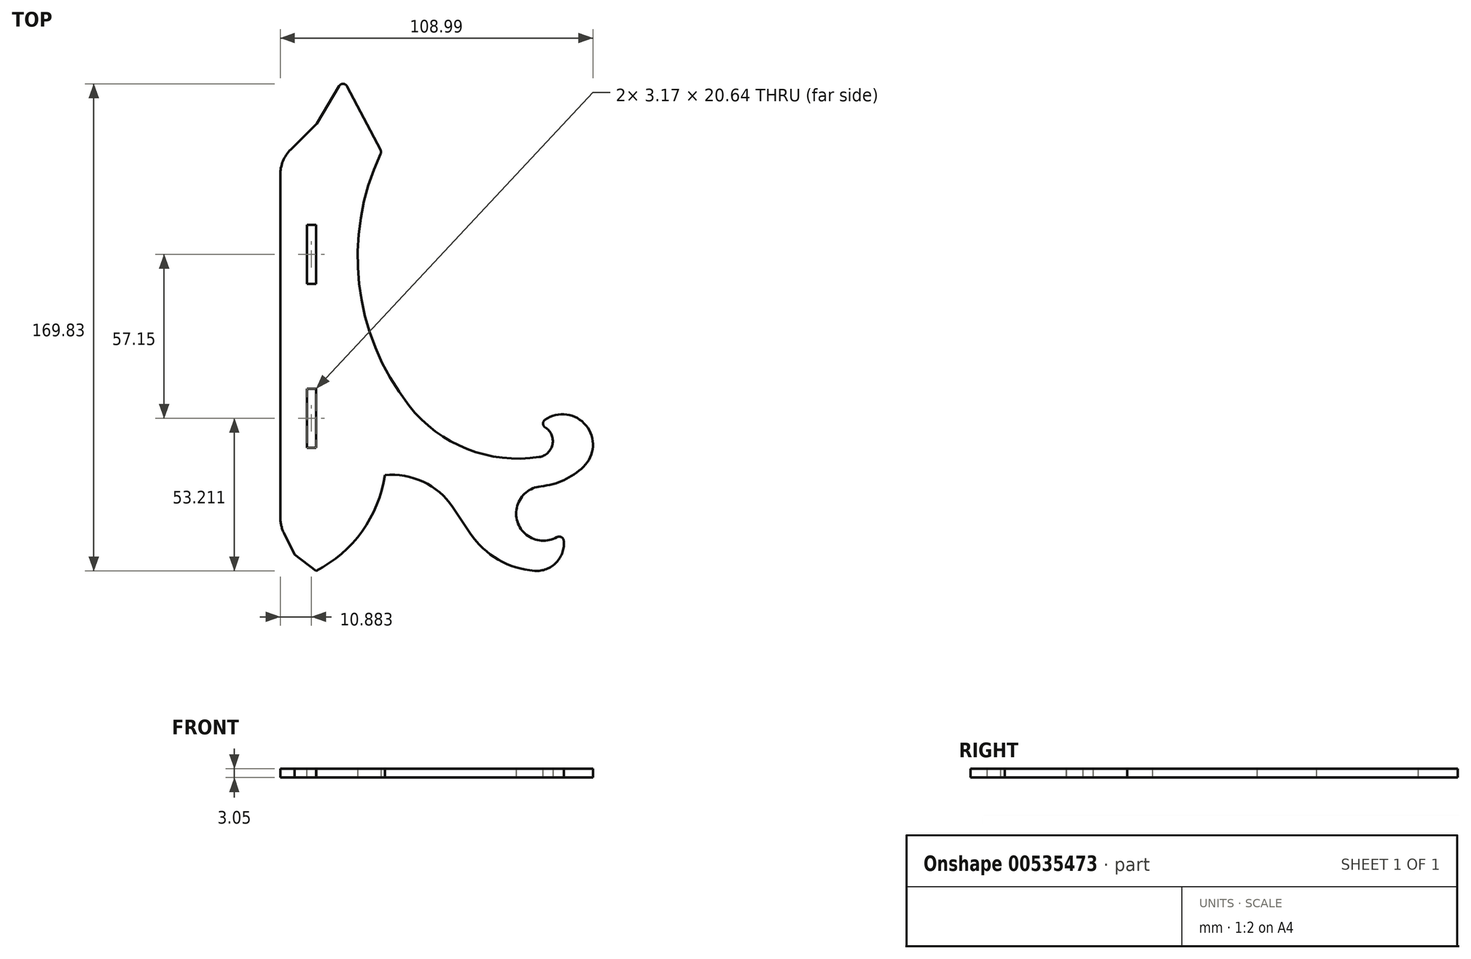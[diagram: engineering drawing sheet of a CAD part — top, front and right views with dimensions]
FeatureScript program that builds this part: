
annotation { "Feature Type Name" : "Feature", "Feature Type Description" : "" }
export const myFeature = defineFeature(function(context is Context, id is Id, definition is map)
    precondition{}
    {
        {
            var Q0;
            Q0=qCreatedBy(makeId("Top.planeOp"),FACE);
            var sketch = newSketch(context, id + "F0", { "sketchPlane" : qUnion([Q0])});
            skLineSegment(sketch, "E0", {"start": v(0, 0) * mm, "end": v(0, 155.58) * mm});
            skLineSegment(sketch, "E1", {"start": v(0, 155.58) * mm, "end": v(9.52, 171.45) * mm});
            skLineSegment(sketch, "E2", {"start": v(9.53, 171.45) * mm, "end": v(22.86, 146.05) * mm});
            skArc(sketch, "E3", {"start": v(0, 0) * mm, "mid": v(16.07, 13.73) * mm, "end": v(23.97, 33.34) * mm});
            skArc(sketch, "E4", {"start": v(47.62, 22.23) * mm, "mid": v(37.34, 31.06) * mm, "end": v(23.97, 33.34) * mm});
            skLineSegment(sketch, "E5", {"start": v(47.62, 22.23) * mm, "end": v(53.82, 13) * mm});
            skArc(sketch, "E6", {"start": v(53.82, 13) * mm, "mid": v(63.51, 3.92) * mm, "end": v(76.2, 0) * mm});
            skArc(sketch, "E7", {"start": v(76.2, 0) * mm, "mid": v(84.56, 3.86) * mm, "end": v(85.73, 13) * mm});
            skArc(sketch, "E8", {"start": v(78.35, 29.47) * mm, "mid": v(70.6, 16.1) * mm, "end": v(85.72, 13) * mm});
            skArc(sketch, "E9", {"start": v(78.35, 29.47) * mm, "mid": v(86.36, 31.63) * mm, "end": v(93.22, 36.28) * mm});
            skArc(sketch, "E10", {"start": v(22.86, 146.05) * mm, "mid": v(15, 100.47) * mm, "end": v(32.42, 57.61) * mm});
            skArc(sketch, "E11", {"start": v(32.42, 57.61) * mm, "mid": v(52.67, 42.5) * mm, "end": v(77.79, 39.69) * mm});
            skArc(sketch, "E12", {"start": v(77.79, 39.69) * mm, "mid": v(82.55, 45.24) * mm, "end": v(77.79, 50.8) * mm});
            skArc(sketch, "E13", {"start": v(93.22, 36.28) * mm, "mid": v(93.18, 51.7) * mm, "end": v(77.79, 50.8) * mm});
            skSolve(sketch);
        }
        {
            var Q0;
            Q0=makeQuery(id+"F0.imprint","IMPRINT",FACE,{"disambiguationData":[TD([[makeQuery(id+"F0.imprint","IMPRINT",EDGE,{"derivedFrom":sQuery(id+"F0.wireOp",EDGE,"E0")}),-1.0]])]});
            extrude(context, id + "F1", {"entities" : qUnion([Q0]), "depth" : 3.05 * mm, "offsetDistance" : 25.4 * mm});
        }
        {
            var Q0;
            Q0=makeQuery(id+"F1.opExtrude","SWEPT_EDGE",EDGE,{"disambiguationData":[OSD([sQuery(id+"F0.wireOp",EDGE,"E7"),sQuery(id+"F0.wireOp",EDGE,"E8")])]});
            var Q1;
            Q1=makeQuery(id+"F1.opExtrude","SWEPT_EDGE",EDGE,{"disambiguationData":[OSD([sQuery(id+"F0.wireOp",EDGE,"E2"),sQuery(id+"F0.wireOp",EDGE,"E10")])]});
            var Q2;
            Q2=makeQuery(id+"F1.opExtrude","SWEPT_EDGE",EDGE,{"disambiguationData":[OSD([sQuery(id+"F0.wireOp",EDGE,"E1"),sQuery(id+"F0.wireOp",EDGE,"E2")])]});
            var Q3;
            Q3=makeQuery(id+"F1.opExtrude","SWEPT_EDGE",EDGE,{"disambiguationData":[OSD([sQuery(id+"F0.wireOp",EDGE,"E0"),sQuery(id+"F0.wireOp",EDGE,"E1")])]});
            var Q4;
            Q4=makeQuery(id+"F1.opExtrude","SWEPT_EDGE",EDGE,{"disambiguationData":[OSD([sQuery(id+"F0.wireOp",EDGE,"E12"),sQuery(id+"F0.wireOp",EDGE,"E13")])]});
            fillet(context, id + "F2", {"entities" : qUnion([Q0, Q1, Q2, Q3, Q4]), "radius" : 1.59 * mm, "tangentPropagation" : true, "allowEdgeOverflow" : false});
        }
        {
            var Q0;
            Q0=makeQuery(id+"F1.opExtrude","SWEPT_BODY",BODY,{"disambiguationData":[OSD([sQuery(id+"F0.wireOp",EDGE,"E0"),sQuery(id+"F0.wireOp",EDGE,"E1"),sQuery(id+"F0.wireOp",EDGE,"E2"),sQuery(id+"F0.wireOp",EDGE,"E3"),sQuery(id+"F0.wireOp",EDGE,"E4"),sQuery(id+"F0.wireOp",EDGE,"E5"),sQuery(id+"F0.wireOp",EDGE,"E6"),sQuery(id+"F0.wireOp",EDGE,"E7"),sQuery(id+"F0.wireOp",EDGE,"E8"),sQuery(id+"F0.wireOp",EDGE,"E9"),sQuery(id+"F0.wireOp",EDGE,"E10"),sQuery(id+"F0.wireOp",EDGE,"E11"),sQuery(id+"F0.wireOp",EDGE,"E12"),sQuery(id+"F0.wireOp",EDGE,"E13")])]});
            transform(context, id + "F3", {"entities" : qUnion([Q0]), "transformType" : TransformType.TRANSLATION_3D, "dx" : 0 * mm, "dy" : 0 * mm, "dz" : 0 * mm, "makeCopy" : true});
        }
        {
            var Q0;
            Q0=makeQuery(id+"F1.opExtrude","CAP_FACE",FACE,{"disambiguationData":[OSD([sQuery(id+"F0.wireOp",EDGE,"E0"),sQuery(id+"F0.wireOp",EDGE,"E1"),sQuery(id+"F0.wireOp",EDGE,"E2"),sQuery(id+"F0.wireOp",EDGE,"E3"),sQuery(id+"F0.wireOp",EDGE,"E4"),sQuery(id+"F0.wireOp",EDGE,"E5"),sQuery(id+"F0.wireOp",EDGE,"E6"),sQuery(id+"F0.wireOp",EDGE,"E7"),sQuery(id+"F0.wireOp",EDGE,"E8"),sQuery(id+"F0.wireOp",EDGE,"E9"),sQuery(id+"F0.wireOp",EDGE,"E10"),sQuery(id+"F0.wireOp",EDGE,"E11"),sQuery(id+"F0.wireOp",EDGE,"E12"),sQuery(id+"F0.wireOp",EDGE,"E13")])],"isStart":false});
            var sketch = newSketch(context, id + "F4", { "sketchPlane" : qUnion([Q0])});
            skLineSegment(sketch, "E14", {"start": v(-12.7, 120.65) * mm, "end": v(-12.7, 100.01) * mm});
            skLineSegment(sketch, "E15", {"start": v(-3.18, 100.01) * mm, "end": v(-3.18, 106.36) * mm});
            skLineSegment(sketch, "E16", {"start": v(-3.18, 106.36) * mm, "end": v(0, 106.36) * mm});
            skLineSegment(sketch, "E17", {"start": v(0, 120.65) * mm, "end": v(0, 106.36) * mm});
            skLineSegment(sketch, "E18", {"start": v(-12.7, 63.5) * mm, "end": v(-12.7, 42.86) * mm});
            skLineSegment(sketch, "E19", {"start": v(-3.18, 42.86) * mm, "end": v(-3.18, 49.21) * mm});
            skLineSegment(sketch, "E20", {"start": v(-3.18, 49.21) * mm, "end": v(0, 49.21) * mm});
            skLineSegment(sketch, "E21", {"start": v(0, 49.21) * mm, "end": v(0, 63.5) * mm});
            skLineSegment(sketch, "E22.bottom", {"start": v(-3.18, 100.01) * mm, "end": v(0, 100.01) * mm});
            skLineSegment(sketch, "E22.top", {"start": v(-3.18, 120.65) * mm, "end": v(0, 120.65) * mm});
            skLineSegment(sketch, "E22.left", {"start": v(-3.18, 100.01) * mm, "end": v(-3.18, 120.65) * mm});
            skLineSegment(sketch, "E22.right", {"start": v(0, 100.01) * mm, "end": v(0, 120.65) * mm});
            skLineSegment(sketch, "E23.bottom", {"start": v(0, 63.5) * mm, "end": v(-3.18, 63.5) * mm});
            skLineSegment(sketch, "E23.top", {"start": v(0, 42.86) * mm, "end": v(-3.18, 42.86) * mm});
            skLineSegment(sketch, "E23.left", {"start": v(0, 63.5) * mm, "end": v(0, 42.86) * mm});
            skLineSegment(sketch, "E23.right", {"start": v(-3.18, 63.5) * mm, "end": v(-3.18, 42.86) * mm});
            skLineSegment(sketch, "E24.bottom", {"start": v(0.23, 155.96) * mm, "end": v(-12.47, 155.96) * mm});
            skLineSegment(sketch, "E24.top", {"start": v(0.23, 9.53) * mm, "end": v(-12.47, 9.53) * mm});
            skLineSegment(sketch, "E24.left", {"start": v(0.23, 155.96) * mm, "end": v(0.23, 9.53) * mm});
            skLineSegment(sketch, "E24.right", {"start": v(-12.47, 155.96) * mm, "end": v(-12.47, 9.53) * mm});
            skLineSegment(sketch, "E25", {"start": v(-12.47, 9.53) * mm, "end": v(0, 0) * mm});
            skSolve(sketch);
        }
        {
            var Q0;
            {var subQ4=sQuery(id+"F4.wireOp",EDGE,"E22.bottom");Q0=makeQuery(id+"F4.imprint","IMPRINT",FACE,{"disambiguationData":[TD([[makeQuery(id+"F4.imprint","IMPRINT",EDGE,{"derivedFrom":subQ4}),-1.0]])]});}
            var Q1;
            {var subQ0=sQuery(id+"F4.wireOp",EDGE,"E25");Q1=makeQuery(id+"F4.imprint","IMPRINT",FACE,{"disambiguationData":[TD([[makeQuery(id+"F4.imprint","IMPRINT",EDGE,{"derivedFrom":subQ0}),1.0]])]});}
            extrude(context, id + "F5", {"entities" : qUnion([Q0, Q1]), "operationType" : NewBodyOperationType.ADD, "oppositeDirection" : true, "depth" : 3.05 * mm, "offsetDistance" : 25.4 * mm});
        }
        {
            var Q0;
            Q0=makeQuery(id+"F5.opExtrude","SWEPT_EDGE",EDGE,{"disambiguationData":[OSD([sQuery(id+"F4.wireOp",EDGE,"E24.bottom"),sQuery(id+"F4.wireOp",EDGE,"E24.right")])]});
            chamfer(context, id + "F6", {"entities" : qUnion([Q0]), "width" : 12.7 * mm, "tangentPropagation" : true});
        }
        {
            var Q0;
            Q0=makeQuery(id+"F5.opExtrude","SWEPT_EDGE",EDGE,{"disambiguationData":[OSD([sQuery(id+"F4.wireOp",EDGE,"E24.top"),sQuery(id+"F4.wireOp",EDGE,"E24.right"),sQuery(id+"F4.wireOp",EDGE,"E25")])]});
            chamfer(context, id + "F7", {"entities" : qUnion([Q0]), "width" : 12.7 * mm, "tangentPropagation" : true});
        }
        {
            var Q0;
            {var subQ0=sQuery(id+"F4.wireOp",EDGE,"E24.right");Q0=makeQuery(id+"F6.opChamfer","BLEND_EDGE",EDGE,{"blendedFrom":[makeQuery(id+"F5.opExtrude","SWEPT_EDGE",EDGE,{"disambiguationData":[OSD([sQuery(id+"F4.wireOp",EDGE,"E24.bottom"),subQ0])]}),makeQuery(id+"F5.opExtrude","SWEPT_FACE",FACE,{"disambiguationData":[OSD([subQ0])]})],"blendedInto":[makeQuery(id+"F5.opExtrude","SWEPT_FACE",FACE,{"disambiguationData":[OSD([subQ0])]})]});}
            var Q1;
            {var subQ0=sQuery(id+"F4.wireOp",EDGE,"E24.right");Q1=makeQuery(id+"F7.opChamfer","BLEND_EDGE",EDGE,{"blendedFrom":[makeQuery(id+"F5.opExtrude","SWEPT_EDGE",EDGE,{"disambiguationData":[OSD([sQuery(id+"F4.wireOp",EDGE,"E24.top"),subQ0,sQuery(id+"F4.wireOp",EDGE,"E25")])]}),makeQuery(id+"F5.opExtrude","SWEPT_FACE",FACE,{"disambiguationData":[OSD([subQ0])]})],"blendedInto":[makeQuery(id+"F5.opExtrude","SWEPT_FACE",FACE,{"disambiguationData":[OSD([subQ0])]})]});}
            fillet(context, id + "F8", {"entities" : qUnion([Q0, Q1]), "radius" : 12.7 * mm, "tangentPropagation" : true, "allowEdgeOverflow" : false});
        }
    });
